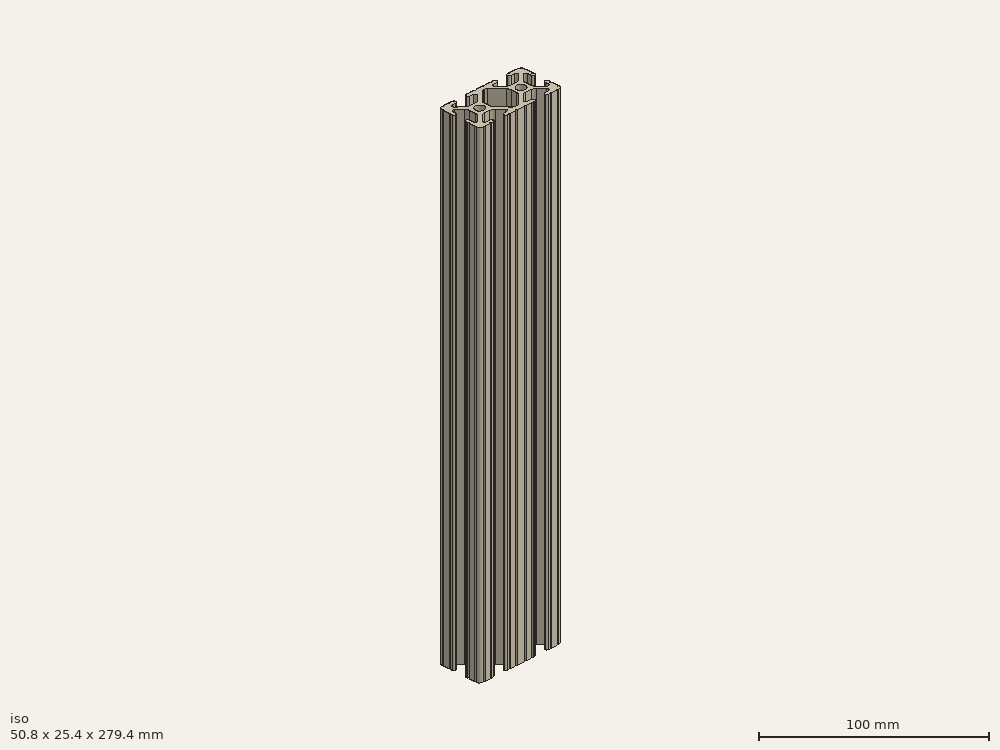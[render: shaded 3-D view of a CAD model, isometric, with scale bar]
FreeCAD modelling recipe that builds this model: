
FCSTD DOCUMENT  (FreeCAD 0.19R24267 (Git))
Label: 1020-11
License: All rights reserved
LicenseURL: http://en.wikipedia.org/wiki/All_rights_reserved
objects: Sketcher::SketchObject×1, Part::Extrusion×1
note: 2 computed .brp shape members not serialized (recipe doc carries the construction recipe); baked Part::Feature solids carry a one-line shape summary decoded from their .brp

FEATURE [Sketcher::SketchObject] Sketch162
  FullyConstrained = false
  sketch-geometry (162):
    g0: LineSegment StartX=7.25951 StartY=3.86941 StartZ=0 EndX=1.54575 EndY=9.57277 EndZ=0
    g1: LineSegment StartX=8.41248 StartY=-10.4902 StartZ=0 EndX=6.28364 EndY=-10.4902 EndZ=0
    g2: ArcOfCircle CenterX=8.41255 CenterY=-11.651 CenterZ=0 NormalX=0 NormalY=0 NormalZ=1 AngleXU=0 Radius=1.04895 StartAngle=4.71239 EndAngle=6.28319
    g3: LineSegment StartX=5.53258 StartY=-8.66607 StartZ=0 EndX=8.80999 EndY=-5.41626 EndZ=0
    g4: LineSegment StartX=9.4615 StartY=-11.651 StartZ=0 EndX=9.4615 EndY=-11.5392 EndZ=0
    g5: ArcOfCircle CenterX=8.41248 CenterY=-11.5392 CenterZ=0 NormalX=0 NormalY=0 NormalZ=1 AngleXU=0 Radius=1.04902 StartAngle=1.15714e-07 EndAngle=1.5708
    g6: ArcOfCircle CenterX=6.28364 CenterY=-9.42351 CenterZ=0 NormalX=0 NormalY=0 NormalZ=1 AngleXU=0 Radius=1.06669 StartAngle=2.35197 EndAngle=4.71239
    g7: LineSegment StartX=-7.28286 StartY=-3.84586 StartZ=0 EndX=-1.67557 EndY=-9.56109 EndZ=0
    g8: LineSegment StartX=1.50403 StartY=-9.57645 StartZ=0 EndX=7.25205 EndY=-3.87684 EndZ=0
    g9: LineSegment StartX=-0.551457 StartY=-10.033 StartZ=0 EndX=0.3952 EndY=-10.033 EndZ=0
    g10: LineSegment StartX=-1.54575 StartY=9.57277 StartZ=0 EndX=-7.25951 EndY=3.86941 EndZ=0
    g11: ArcOfCircle CenterX=0.3952 CenterY=-8.4582 CenterZ=0 NormalX=0 NormalY=0 NormalZ=1 AngleXU=0 Radius=1.5748 StartAngle=4.71239 EndAngle=5.49356
    g12: ArcOfCircle CenterX=5.0165 CenterY=-1.6223 CenterZ=0 NormalX=0 NormalY=0 NormalZ=1 AngleXU=0 Radius=3.175 StartAngle=5.49356 EndAngle=6.28319
    g13: LineSegment StartX=8.1915 StartY=-1.6223 StartZ=0 EndX=8.1915 EndY=1.6223 EndZ=0
    g14: LineSegment StartX=0.433213 StartY=10.033 StartZ=0 EndX=-0.433213 EndY=10.033 EndZ=0
    g15: ArcOfCircle CenterX=-0.551456 CenterY=-8.4582 CenterZ=0 NormalX=0 NormalY=0 NormalZ=1 AngleXU=0 Radius=1.5748 StartAngle=3.91746 EndAngle=4.71239
    g16: ArcOfCircle CenterX=-5.0165 CenterY=1.6223 CenterZ=0 NormalX=0 NormalY=0 NormalZ=1 AngleXU=0 Radius=3.175 StartAngle=2.35528 EndAngle=3.14159
    g17: ArcOfCircle CenterX=-0.433213 CenterY=8.4582 CenterZ=0 NormalX=0 NormalY=0 NormalZ=1 AngleXU=0 Radius=1.5748 StartAngle=1.5708 EndAngle=2.35528
    g18: ArcOfCircle CenterX=5.0165 CenterY=1.6223 CenterZ=0 NormalX=0 NormalY=0 NormalZ=1 AngleXU=0 Radius=3.175 StartAngle=2.15656e-07 EndAngle=0.78631
    g19: Circle CenterX=12.7 CenterY=-2.5e-15 CenterZ=0 NormalX=0 NormalY=0 NormalZ=-1 AngleXU=0 Radius=2.6035
    g20: Circle CenterX=-12.7 CenterY=2.5e-15 CenterZ=0 NormalX=0 NormalY=0 NormalZ=-1 AngleXU=0 Radius=2.6035
    g21: LineSegment StartX=-8.1915 StartY=1.6223 StartZ=0 EndX=-8.1915 EndY=-1.6223 EndZ=0
    g22: LineSegment StartX=-2.13358 StartY=-12.7 StartZ=0 EndX=2.13358 EndY=-12.7 EndZ=0
    g23: ArcOfCircle CenterX=-5.0165 CenterY=-1.6223 CenterZ=0 NormalX=0 NormalY=0 NormalZ=1 AngleXU=0 Radius=3.175 StartAngle=3.14159 EndAngle=3.91746
    g24: LineSegment StartX=3.14958 StartY=-12.7 StartZ=0 EndX=6.3669 EndY=-12.7 EndZ=0
    g25: ArcOfCircle CenterX=6.8749 CenterY=-12.7 CenterZ=0 NormalX=0 NormalY=0 NormalZ=1 AngleXU=0 Radius=0.508 StartAngle=0 EndAngle=3.14159
    g26: LineSegment StartX=-6.28939 StartY=-10.4902 StartZ=0 EndX=-8.41248 EndY=-10.4902 EndZ=0
    g27: LineSegment StartX=-8.41255 StartY=-12.7 StartZ=0 EndX=-7.38288 EndY=-12.7 EndZ=0
    g28: ArcOfCircle CenterX=0.433213 CenterY=8.4582 CenterZ=0 NormalX=0 NormalY=0 NormalZ=1 AngleXU=0 Radius=1.5748 StartAngle=0.78631 EndAngle=1.5708
    g29: ArcOfCircle CenterX=2.64158 CenterY=-12.7 CenterZ=0 NormalX=0 NormalY=0 NormalZ=1 AngleXU=0 Radius=0.508 StartAngle=0 EndAngle=3.14159
    g30: ArcOfCircle CenterX=-16.9875 CenterY=-11.5392 CenterZ=0 NormalX=0 NormalY=0 NormalZ=1 AngleXU=0 Radius=1.04902 StartAngle=1.16223e-07 EndAngle=1.5708
    g31: LineSegment StartX=-8.81696 StartY=-5.44724 StartZ=0 EndX=-5.56415 EndY=-8.76265 EndZ=0
    g32: LineSegment StartX=-16.9875 StartY=-10.4902 StartZ=0 EndX=-19.1164 EndY=-10.4902 EndZ=0
    g33: ArcOfCircle CenterX=-11.0833 CenterY=-7.6708 CenterZ=0 NormalX=0 NormalY=0 NormalZ=1 AngleXU=0 Radius=3.175 StartAngle=0.775866 EndAngle=1.5708
    g34: ArcOfCircle CenterX=-14.3449 CenterY=-7.6708 CenterZ=0 NormalX=0 NormalY=0 NormalZ=1 AngleXU=0 Radius=3.175 StartAngle=1.5708 EndAngle=2.3692
    g35: ArcOfCircle CenterX=-19.1164 CenterY=-9.4742 CenterZ=0 NormalX=0 NormalY=0 NormalZ=1 AngleXU=0 Radius=1.016 StartAngle=2.3692 EndAngle=4.71239
    g36: ArcOfCircle CenterX=-8.41248 CenterY=-11.5392 CenterZ=0 NormalX=0 NormalY=0 NormalZ=1 AngleXU=0 Radius=1.04902 StartAngle=1.5708 EndAngle=3.14159
    g37: LineSegment StartX=7.3829 StartY=-12.7 StartZ=0 EndX=8.41255 EndY=-12.7 EndZ=0
    g38: ArcOfCircle CenterX=-8.41255 CenterY=-11.651 CenterZ=0 NormalX=0 NormalY=0 NormalZ=1 AngleXU=0 Radius=1.04895 StartAngle=3.14159 EndAngle=4.71239
    g39: ArcOfCircle CenterX=14.3545 CenterY=-7.6708 CenterZ=0 NormalX=0 NormalY=0 NormalZ=1 AngleXU=0 Radius=3.175 StartAngle=0.789627 EndAngle=1.5708
    g40: ArcOfCircle CenterX=20.3835 CenterY=-1.55362 CenterZ=0 NormalX=0 NormalY=0 NormalZ=1 AngleXU=0 Radius=3.175 StartAngle=3.14159 EndAngle=3.93122
    g41: LineSegment StartX=23.1902 StartY=6.498 StartZ=0 EndX=23.1902 EndY=4.28752 EndZ=0
    g42: LineSegment StartX=-14.3449 StartY=-4.4958 StartZ=0 EndX=-11.0833 EndY=-4.4958 EndZ=0
    g43: LineSegment StartX=-19.8441 StartY=-8.76517 StartZ=0 EndX=-16.619 EndY=-5.45511 EndZ=0
    g44: LineSegment StartX=-6.36688 StartY=-12.7 StartZ=0 EndX=-3.14958 EndY=-12.7 EndZ=0
    g45: ArcOfCircle CenterX=-6.28939 CenterY=-9.4742 CenterZ=0 NormalX=0 NormalY=0 NormalZ=1 AngleXU=0 Radius=1.016 StartAngle=4.71239 EndAngle=7.05905
    g46: LineSegment StartX=-9.4615 StartY=-11.5392 StartZ=0 EndX=-9.4615 EndY=-11.6511 EndZ=0
    g47: ArcOfCircle CenterX=-6.87488 CenterY=-12.7 CenterZ=0 NormalX=0 NormalY=0 NormalZ=1 AngleXU=0 Radius=0.508 StartAngle=0 EndAngle=3.14159
    g48: LineSegment StartX=-15.9385 StartY=-11.651 StartZ=0 EndX=-15.9385 EndY=-11.5392 EndZ=0
    g49: ArcOfCircle CenterX=-2.64158 CenterY=-12.7 CenterZ=0 NormalX=0 NormalY=0 NormalZ=1 AngleXU=0 Radius=0.508 StartAngle=0 EndAngle=3.14159
    g50: ArcOfCircle CenterX=22.1596 CenterY=-6.33474 CenterZ=0 NormalX=0 NormalY=0 NormalZ=1 AngleXU=0 Radius=1.03057 StartAngle=3.93122 EndAngle=6.28319
    g51: ArcOfCircle CenterX=25.4 CenterY=5.82513 CenterZ=0 NormalX=0 NormalY=0 NormalZ=1 AngleXU=0 Radius=0.508 StartAngle=1.5708 EndAngle=4.71239
    g52: LineSegment StartX=25.4 StartY=6.33313 StartZ=0 EndX=25.4 EndY=9.5504 EndZ=0
    g53: LineSegment StartX=19.0331 StartY=-12.7 StartZ=0 EndX=22.2504 EndY=-12.7 EndZ=0
    g54: ArcOfCircle CenterX=20.3835 CenterY=1.69518 CenterZ=0 NormalX=0 NormalY=0 NormalZ=1 AngleXU=0 Radius=3.175 StartAngle=2.35528 EndAngle=3.14159
    g55: LineSegment StartX=16.9875 StartY=-12.7 StartZ=0 EndX=18.0171 EndY=-12.7 EndZ=0
    g56: ArcOfCircle CenterX=23.2918 CenterY=10.5918 CenterZ=0 NormalX=0 NormalY=0 NormalZ=1 AngleXU=0 Radius=2.1082 StartAngle=6.27114 EndAngle=7.86603
    g57: ArcOfCircle CenterX=24.2392 CenterY=-4.28752 CenterZ=0 NormalX=0 NormalY=0 NormalZ=1 AngleXU=0 Radius=1.04902 StartAngle=1.5708 EndAngle=3.14159
    g58: ArcOfCircle CenterX=24.401 CenterY=-4.23752 CenterZ=0 NormalX=0 NormalY=0 NormalZ=1 AngleXU=0 Radius=0.99902 StartAngle=1.41033e-07 EndAngle=1.5708
    g59: LineSegment StartX=16.59 StartY=-5.41626 StartZ=0 EndX=19.8674 EndY=-8.66607 EndZ=0
    g60: ArcOfCircle CenterX=16.9875 CenterY=-11.5392 CenterZ=0 NormalX=0 NormalY=0 NormalZ=1 AngleXU=0 Radius=1.04902 StartAngle=1.5708 EndAngle=3.14159
    g61: LineSegment StartX=22.2504 StartY=12.7 StartZ=0 EndX=19.0331 EndY=12.7 EndZ=0
    g62: ArcOfCircle CenterX=23.2918 CenterY=-10.5918 CenterZ=0 NormalX=0 NormalY=0 NormalZ=1 AngleXU=0 Radius=2.1082 StartAngle=4.70034 EndAngle=6.29523
    g63: ArcOfCircle CenterX=11.0455 CenterY=-7.6708 CenterZ=0 NormalX=0 NormalY=0 NormalZ=1 AngleXU=0 Radius=3.175 StartAngle=1.5708 EndAngle=2.35197
    g64: ArcOfCircle CenterX=22.7584 CenterY=12.7 CenterZ=0 NormalX=0 NormalY=0 NormalZ=1 AngleXU=0 Radius=0.508 StartAngle=3.14159 EndAngle=6.28288
    g65: LineSegment StartX=19.1164 StartY=-10.4902 StartZ=0 EndX=16.9875 EndY=-10.4902 EndZ=0
    g66: ArcOfCircle CenterX=22.7584 CenterY=-12.7 CenterZ=0 NormalX=0 NormalY=0 NormalZ=1 AngleXU=0 Radius=0.508 StartAngle=0.000301216 EndAngle=3.14159
    g67: ArcOfCircle CenterX=16.9875 CenterY=11.651 CenterZ=0 NormalX=0 NormalY=0 NormalZ=1 AngleXU=0 Radius=1.04902 StartAngle=1.5708 EndAngle=3.14159
    g68: ArcOfCircle CenterX=24.351 CenterY=4.28752 CenterZ=0 NormalX=0 NormalY=0 NormalZ=1 AngleXU=0 Radius=1.04902 StartAngle=4.71239 EndAngle=6.28319
    g69: ArcOfCircle CenterX=19.1164 CenterY=9.4742 CenterZ=0 NormalX=0 NormalY=0 NormalZ=1 AngleXU=0 Radius=1.016 StartAngle=5.49688 EndAngle=7.85398
    g70: LineSegment StartX=19.8341 StartY=8.75512 StartZ=0 EndX=16.4966 EndY=5.42369 EndZ=0
    g71: LineSegment StartX=18.0171 StartY=12.7 StartZ=0 EndX=16.9875 EndY=12.7 EndZ=0
    g72: ArcOfCircle CenterX=18.5251 CenterY=-12.7 CenterZ=0 NormalX=0 NormalY=0 NormalZ=1 AngleXU=0 Radius=0.508 StartAngle=0 EndAngle=3.14159
    g73: LineSegment StartX=15.9384 StartY=11.651 StartZ=0 EndX=15.9384 EndY=11.5392 EndZ=0
    g74: LineSegment StartX=16.9875 StartY=10.4902 StartZ=0 EndX=19.1164 EndY=10.4902 EndZ=0
    g75: LineSegment StartX=11.0455 StartY=-4.4958 StartZ=0 EndX=14.3545 EndY=-4.4958 EndZ=0
    g76: ArcOfCircle CenterX=14.2536 CenterY=7.6708 CenterZ=0 NormalX=0 NormalY=0 NormalZ=1 AngleXU=0 Radius=3.175 StartAngle=4.71239 EndAngle=5.49688
    g77: ArcOfCircle CenterX=25.4 CenterY=-5.82508 CenterZ=0 NormalX=0 NormalY=0 NormalZ=1 AngleXU=0 Radius=0.508 StartAngle=1.5708 EndAngle=4.71239
    g78: LineSegment StartX=18.1405 StartY=3.94229 StartZ=0 EndX=21.4316 EndY=7.22739 EndZ=0
    g79: LineSegment StartX=25.4 StartY=-5.31708 StartZ=0 EndX=25.4 EndY=-4.23752 EndZ=0
    g80: LineSegment StartX=14.2536 StartY=4.4958 StartZ=0 EndX=11.1464 EndY=4.4958 EndZ=0
    g81: ArcOfCircle CenterX=18.5251 CenterY=12.7 CenterZ=0 NormalX=0 NormalY=0 NormalZ=1 AngleXU=0 Radius=0.508 StartAngle=3.14159 EndAngle=6.28319
    g82: LineSegment StartX=23.1902 StartY=-4.28752 StartZ=0 EndX=23.1902 EndY=-6.33474 EndZ=0
    g83: LineSegment StartX=24.401 StartY=-3.2385 StartZ=0 EndX=24.2392 EndY=-3.2385 EndZ=0
    g84: ArcOfCircle CenterX=22.1596 CenterY=6.498 CenterZ=0 NormalX=0 NormalY=0 NormalZ=1 AngleXU=0 Radius=1.03057 StartAngle=0 EndAngle=2.35528
    g85: LineSegment StartX=15.9385 StartY=-11.5392 StartZ=0 EndX=15.9385 EndY=-11.6511 EndZ=0
    g86: LineSegment StartX=25.4 StartY=4.28752 StartZ=0 EndX=25.4 EndY=5.31713 EndZ=0
    g87: ArcOfCircle CenterX=11.1464 CenterY=7.6708 CenterZ=0 NormalX=0 NormalY=0 NormalZ=1 AngleXU=0 Radius=3.175 StartAngle=3.9279 EndAngle=4.71239
    g88: LineSegment StartX=8.90339 StartY=5.42369 StartZ=0 EndX=5.56588 EndY=8.75512 EndZ=0
    g89: LineSegment StartX=21.434 StartY=-7.06654 StartZ=0 EndX=18.148 EndY=-3.80816 EndZ=0
    g90: ArcOfCircle CenterX=25.4 CenterY=10.0584 CenterZ=0 NormalX=0 NormalY=0 NormalZ=1 AngleXU=0 Radius=0.508 StartAngle=1.5711 EndAngle=4.71239
    g91: ArcOfCircle CenterX=16.9875 CenterY=-11.651 CenterZ=0 NormalX=0 NormalY=0 NormalZ=1 AngleXU=0 Radius=1.04895 StartAngle=3.14159 EndAngle=4.71239
    g92: ArcOfCircle CenterX=19.1164 CenterY=-9.42352 CenterZ=0 NormalX=0 NormalY=0 NormalZ=1 AngleXU=0 Radius=1.06668 StartAngle=4.71239 EndAngle=7.07281
    g93: ArcOfCircle CenterX=24.2392 CenterY=4.28752 CenterZ=0 NormalX=0 NormalY=0 NormalZ=1 AngleXU=0 Radius=1.04902 StartAngle=3.14159 EndAngle=4.71239
    g94: ArcOfCircle CenterX=16.9875 CenterY=11.5392 CenterZ=0 NormalX=0 NormalY=0 NormalZ=1 AngleXU=0 Radius=1.04902 StartAngle=3.14159 EndAngle=4.71239
    g95: ArcOfCircle CenterX=25.4 CenterY=-10.0584 CenterZ=0 NormalX=0 NormalY=0 NormalZ=1 AngleXU=0 Radius=0.508 StartAngle=1.5708 EndAngle=4.71209
    g96: ArcOfCircle CenterX=6.87487 CenterY=12.7 CenterZ=0 NormalX=0 NormalY=0 NormalZ=1 AngleXU=0 Radius=0.508 StartAngle=3.14159 EndAngle=6.28319
    g97: LineSegment StartX=25.4 StartY=-9.5504 StartZ=0 EndX=25.4 EndY=-6.33308 EndZ=0
    g98: LineSegment StartX=17.2085 StartY=-1.55362 StartZ=0 EndX=17.2085 EndY=1.69518 EndZ=0
    g99: LineSegment StartX=-9.46155 StartY=11.651 StartZ=0 EndX=-9.46155 EndY=11.5392 EndZ=0
    g100: LineSegment StartX=24.2392 StartY=3.2385 StartZ=0 EndX=24.351 EndY=3.2385 EndZ=0
    g101: LineSegment StartX=-8.41253 StartY=10.4902 StartZ=0 EndX=-6.28939 EndY=10.4902 EndZ=0
    g102: ArcOfCircle CenterX=-10.8409 CenterY=7.6708 CenterZ=0 NormalX=0 NormalY=0 NormalZ=1 AngleXU=0 Radius=3.175 StartAngle=4.71239 EndAngle=5.49688
    g103: LineSegment StartX=-19.1164 StartY=10.4902 StartZ=0 EndX=-16.9875 EndY=10.4902 EndZ=0
    g104: LineSegment StartX=-10.8409 StartY=4.4958 StartZ=0 EndX=-14.1026 EndY=4.4958 EndZ=0
    g105: LineSegment StartX=-16.1879 StartY=5.27664 StartZ=0 EndX=-19.8682 EndY=8.48225 EndZ=0
    g106: LineSegment StartX=-7.38291 StartY=12.7 StartZ=0 EndX=-8.41253 EndY=12.7 EndZ=0
    g107: ArcOfCircle CenterX=-6.28939 CenterY=9.34546 CenterZ=0 NormalX=0 NormalY=0 NormalZ=1 AngleXU=0 Radius=1.14474 StartAngle=5.49688 EndAngle=7.85398
    g108: LineSegment StartX=6.28364 StartY=10.4902 StartZ=0 EndX=8.41253 EndY=10.4902 EndZ=0
    g109: ArcOfCircle CenterX=8.41253 CenterY=11.651 CenterZ=0 NormalX=0 NormalY=0 NormalZ=1 AngleXU=0 Radius=1.04902 StartAngle=4.29175e-07 EndAngle=1.5708
    g110: LineSegment StartX=9.46155 StartY=11.5392 StartZ=0 EndX=9.46155 EndY=11.651 EndZ=0
    g111: ArcOfCircle CenterX=-14.1026 CenterY=7.6708 CenterZ=0 NormalX=0 NormalY=0 NormalZ=1 AngleXU=0 Radius=3.175 StartAngle=3.99583 EndAngle=4.71239
    g112: LineSegment StartX=-5.48068 StartY=8.53527 StartZ=0 EndX=-8.59793 EndY=5.42369 EndZ=0
    g113: ArcOfCircle CenterX=-19.1164 CenterY=9.34546 CenterZ=0 NormalX=0 NormalY=0 NormalZ=1 AngleXU=0 Radius=1.14474 StartAngle=1.5708 EndAngle=3.99583
    g114: LineSegment StartX=8.41253 StartY=12.7 StartZ=0 EndX=7.38287 EndY=12.7 EndZ=0
    g115: LineSegment StartX=-3.14958 StartY=12.7 StartZ=0 EndX=-6.36691 EndY=12.7 EndZ=0
    g116: ArcOfCircle CenterX=-8.41253 CenterY=11.5392 CenterZ=0 NormalX=0 NormalY=0 NormalZ=1 AngleXU=0 Radius=1.04902 StartAngle=3.14159 EndAngle=4.71239
    g117: ArcOfCircle CenterX=8.41253 CenterY=11.5392 CenterZ=0 NormalX=0 NormalY=0 NormalZ=1 AngleXU=0 Radius=1.04902 StartAngle=4.71239 EndAngle=6.28319
    g118: ArcOfCircle CenterX=-6.87491 CenterY=12.7 CenterZ=0 NormalX=0 NormalY=0 NormalZ=1 AngleXU=0 Radius=0.508 StartAngle=3.14159 EndAngle=6.28319
    g119: ArcOfCircle CenterX=-8.41253 CenterY=11.651 CenterZ=0 NormalX=0 NormalY=0 NormalZ=1 AngleXU=0 Radius=1.04902 StartAngle=1.5708 EndAngle=3.14159
    g120: ArcOfCircle CenterX=-2.64159 CenterY=12.7 CenterZ=0 NormalX=0 NormalY=0 NormalZ=1 AngleXU=0 Radius=0.507987 StartAngle=3.14159 EndAngle=6.28319
    g121: ArcOfCircle CenterX=6.28364 CenterY=9.4742 CenterZ=0 NormalX=0 NormalY=0 NormalZ=1 AngleXU=0 Radius=1.016 StartAngle=1.5708 EndAngle=3.9279
    g122: LineSegment StartX=2.13361 StartY=12.7 StartZ=0 EndX=-2.13361 EndY=12.7 EndZ=0
    g123: LineSegment StartX=6.36687 StartY=12.7 StartZ=0 EndX=3.14961 EndY=12.7 EndZ=0
    g124: ArcOfCircle CenterX=-24.401 CenterY=4.23752 CenterZ=0 NormalX=0 NormalY=0 NormalZ=1 AngleXU=0 Radius=0.99902 StartAngle=3.14159 EndAngle=4.71239
    g125: LineSegment StartX=-16.9875 StartY=12.7 StartZ=0 EndX=-18.0171 EndY=12.7 EndZ=0
    g126: LineSegment StartX=-24.401 StartY=3.2385 StartZ=0 EndX=-24.1892 EndY=3.2385 EndZ=0
    g127: ArcOfCircle CenterX=2.64161 CenterY=12.7 CenterZ=0 NormalX=0 NormalY=0 NormalZ=1 AngleXU=0 Radius=0.508 StartAngle=3.14159 EndAngle=6.28319
    g128: ArcOfCircle CenterX=-22.2207 CenterY=-6.67687 CenterZ=0 NormalX=0 NormalY=0 NormalZ=1 AngleXU=0 Radius=0.969476 StartAngle=3.14159 EndAngle=5.51079
    g129: LineSegment StartX=-18.1094 StartY=-3.8465 StartZ=0 EndX=-21.5263 EndY=-7.35342 EndZ=0
    g130: LineSegment StartX=-17.2085 StartY=1.63081 StartZ=0 EndX=-17.2085 EndY=-1.63081 EndZ=0
    g131: ArcOfCircle CenterX=-22.2207 CenterY=6.15588 CenterZ=0 NormalX=0 NormalY=0 NormalZ=1 AngleXU=0 Radius=0.969476 StartAngle=0.854233 EndAngle=3.14159
    g132: LineSegment StartX=-24.1892 StartY=-3.2385 StartZ=0 EndX=-24.401 EndY=-3.2385 EndZ=0
    g133: ArcOfCircle CenterX=-25.4 CenterY=10.0584 CenterZ=0 NormalX=0 NormalY=0 NormalZ=1 AngleXU=0 Radius=0.508 StartAngle=4.71239 EndAngle=7.85368
    g134: LineSegment StartX=-23.1902 StartY=-6.67687 StartZ=0 EndX=-23.1902 EndY=-4.23752 EndZ=0
    g135: ArcOfCircle CenterX=-20.3835 CenterY=-1.63081 CenterZ=0 NormalX=0 NormalY=0 NormalZ=1 AngleXU=0 Radius=3.175 StartAngle=5.51079 EndAngle=6.28319
    g136: ArcOfCircle CenterX=-24.1892 CenterY=-4.23752 CenterZ=0 NormalX=0 NormalY=0 NormalZ=1 AngleXU=0 Radius=0.99902 StartAngle=1.41033e-07 EndAngle=1.5708
    g137: ArcOfCircle CenterX=-25.4 CenterY=5.82508 CenterZ=0 NormalX=0 NormalY=0 NormalZ=1 AngleXU=0 Radius=0.508 StartAngle=4.71239 EndAngle=7.85398
    g138: LineSegment StartX=-23.1902 StartY=4.23752 StartZ=0 EndX=-23.1902 EndY=6.15588 EndZ=0
    g139: LineSegment StartX=-15.9384 StartY=11.5392 StartZ=0 EndX=-15.9384 EndY=11.651 EndZ=0
    g140: ArcOfCircle CenterX=-22.7584 CenterY=12.7 CenterZ=0 NormalX=0 NormalY=0 NormalZ=1 AngleXU=0 Radius=0.508 StartAngle=3.14189 EndAngle=6.28319
    g141: LineSegment StartX=-19.0331 StartY=12.7 StartZ=0 EndX=-22.2504 EndY=12.7 EndZ=0
    g142: ArcOfCircle CenterX=-16.9875 CenterY=11.651 CenterZ=0 NormalX=0 NormalY=0 NormalZ=1 AngleXU=0 Radius=1.04902 StartAngle=4.28571e-07 EndAngle=1.5708
    g143: ArcOfCircle CenterX=-18.5251 CenterY=12.7 CenterZ=0 NormalX=0 NormalY=0 NormalZ=1 AngleXU=0 Radius=0.508 StartAngle=3.14159 EndAngle=6.28319
    g144: ArcOfCircle CenterX=-24.1892 CenterY=4.23752 CenterZ=0 NormalX=0 NormalY=0 NormalZ=1 AngleXU=0 Radius=0.99902 StartAngle=4.71239 EndAngle=6.28319
    g145: LineSegment StartX=-25.4 StartY=5.31708 StartZ=0 EndX=-25.4 EndY=4.23752 EndZ=0
    g146: ArcOfCircle CenterX=-16.9875 CenterY=11.5392 CenterZ=0 NormalX=0 NormalY=0 NormalZ=1 AngleXU=0 Radius=1.04902 StartAngle=4.71239 EndAngle=6.28319
    g147: LineSegment StartX=-21.584 StartY=6.88693 StartZ=0 EndX=-18.2982 EndY=4.02497 EndZ=0
    g148: ArcOfCircle CenterX=-20.3835 CenterY=1.63081 CenterZ=0 NormalX=0 NormalY=0 NormalZ=1 AngleXU=0 Radius=3.175 StartAngle=0 EndAngle=0.854233
    g149: ArcOfCircle CenterX=-23.2918 CenterY=10.5918 CenterZ=0 NormalX=0 NormalY=0 NormalZ=1 AngleXU=0 Radius=2.1082 StartAngle=1.55875 EndAngle=3.15364
    g150: LineSegment StartX=-25.4 StartY=9.5504 StartZ=0 EndX=-25.4 EndY=6.33308 EndZ=0
    g151: LineSegment StartX=-25.4 StartY=-4.23752 StartZ=0 EndX=-25.4 EndY=-5.31708 EndZ=0
    g152: ArcOfCircle CenterX=-23.2918 CenterY=-10.5918 CenterZ=0 NormalX=0 NormalY=0 NormalZ=1 AngleXU=0 Radius=2.1082 StartAngle=3.12954 EndAngle=4.72444
    g153: ArcOfCircle CenterX=-22.7584 CenterY=-12.7 CenterZ=0 NormalX=0 NormalY=0 NormalZ=1 AngleXU=0 Radius=0.508 StartAngle=0 EndAngle=3.14129
    g154: LineSegment StartX=-18.0171 StartY=-12.7 StartZ=0 EndX=-16.9875 EndY=-12.7 EndZ=0
    g155: ArcOfCircle CenterX=-25.4 CenterY=-10.0584 CenterZ=0 NormalX=0 NormalY=0 NormalZ=1 AngleXU=0 Radius=0.508 StartAngle=4.71269 EndAngle=7.85398
    g156: LineSegment StartX=-22.2504 StartY=-12.7 StartZ=0 EndX=-19.0331 EndY=-12.7 EndZ=0
    g157: ArcOfCircle CenterX=-16.9875 CenterY=-11.651 CenterZ=0 NormalX=0 NormalY=0 NormalZ=1 AngleXU=0 Radius=1.04895 StartAngle=4.71239 EndAngle=6.28319
    g158: ArcOfCircle CenterX=-24.401 CenterY=-4.23752 CenterZ=0 NormalX=0 NormalY=0 NormalZ=1 AngleXU=0 Radius=0.99902 StartAngle=1.5708 EndAngle=3.14159
    g159: ArcOfCircle CenterX=-25.4 CenterY=-5.82513 CenterZ=0 NormalX=0 NormalY=0 NormalZ=1 AngleXU=0 Radius=0.508051 StartAngle=4.71239 EndAngle=7.85398
    g160: ArcOfCircle CenterX=-18.5251 CenterY=-12.7 CenterZ=0 NormalX=0 NormalY=0 NormalZ=1 AngleXU=0 Radius=0.508 StartAngle=0 EndAngle=3.14159
    g161: LineSegment StartX=-25.4 StartY=-6.33319 StartZ=0 EndX=-25.4 EndY=-9.5504 EndZ=0
  constraints (160):
    c: Coincident(g161,g155)
    c: Coincident(g159,g161)
    c: Coincident(g151,g159)
    c: Coincident(g158,g151)
    c: Coincident(g124,g145)
    c: Coincident(g137,g145)
    c: Coincident(g137,g150)
    c: Coincident(g133,g150)
    c: Coincident(g152,g155)
    c: Coincident(g149,g133)
    c: Coincident(g158,g132)
    c: Coincident(g124,g126)
    c: Coincident(g136,g132)
    c: Coincident(g144,g126)
    c: Coincident(g153,g152)
    c: Coincident(g140,g149)
    c: Coincident(g134,g128)
    c: Coincident(g134,g136)
    c: Coincident(g138,g144)
    c: Coincident(g131,g138)
    c: Coincident(g153,g156)
    c: Coincident(g141,g140)
    c: Coincident(g131,g147)
    c: Coincident(g129,g128)
    c: Coincident(g105,g113)
    c: Coincident(g35,g43)
    c: Coincident(g35,g32)
    c: Coincident(g113,g103)
    c: Coincident(g156,g160)
    c: Coincident(g143,g141)
    c: Coincident(g147,g148)
    c: Coincident(g135,g129)
    c: Coincident(g154,g160)
    c: Coincident(g143,g125)
    c: Coincident(g130,g135)
    c: Coincident(g130,g148)
    c: Coincident(g154,g157)
    c: Coincident(g32,g30)
    c: Coincident(g103,g146)
    c: Coincident(g142,g125)
    c: Coincident(g43,g34)
    c: Coincident(g111,g105)
    c: Coincident(g157,g48)
    c: Coincident(g48,g30)
    c: Coincident(g139,g146)
    c: Coincident(g139,g142)
    c: Coincident(g42,g34)
    c: Coincident(g104,g111)
    c: Coincident(g33,g42)
    c: Coincident(g102,g104)
    c: Coincident(g38,g46)
    c: Coincident(g46,g36)
    c: Coincident(g99,g116)
    c: Coincident(g119,g99)
    c: Coincident(g33,g31)
    c: Coincident(g102,g112)
    c: Coincident(g27,g38)
    c: Coincident(g36,g26)
    c: Coincident(g116,g101)
    c: Coincident(g106,g119)
    c: Coincident(g21,g23)
    c: Coincident(g21,g16)
    c: Coincident(g27,g47)
    c: Coincident(g106,g118)
    c: Coincident(g23,g7)
    c: Coincident(g10,g16)
    c: Coincident(g44,g47)
    c: Coincident(g118,g115)
    c: Coincident(g45,g26)
    c: Coincident(g107,g101)
    c: Coincident(g45,g31)
    c: Coincident(g112,g107)
    c: Coincident(g44,g49)
    c: Coincident(g120,g115)
    c: Coincident(g22,g49)
    c: Coincident(g122,g120)
    c: Coincident(g15,g7)
    c: Coincident(g10,g17)
    c: Coincident(g9,g15)
    c: Coincident(g17,g14)
    c: Coincident(g9,g11)
    c: Coincident(g14,g28)
    c: Coincident(g8,g11)
    c: Coincident(g0,g28)
    c: Coincident(g29,g22)
    c: Coincident(g122,g127)
    c: Coincident(g24,g29)
    c: Coincident(g123,g127)
    c: Coincident(g3,g6)
    c: Coincident(g88,g121)
    c: Coincident(g1,g6)
    c: Coincident(g108,g121)
    c: Coincident(g25,g24)
    c: Coincident(g96,g123)
    c: Coincident(g8,g12)
    c: Coincident(g18,g0)
    c: Coincident(g25,g37)
    c: Coincident(g96,g114)
    c: Coincident(g12,g13)
    c: Coincident(g18,g13)
    c: Coincident(g2,g37)
    c: Coincident(g5,g1)
    c: Coincident(g117,g108)
    c: Coincident(g109,g114)
    c: Coincident(g3,g63)
    c: Coincident(g87,g88)
    c: Coincident(g2,g4)
    c: Coincident(g5,g4)
    c: Coincident(g117,g110)
    c: Coincident(g109,g110)
    c: Coincident(g75,g63)
    c: Coincident(g80,g87)
    c: Coincident(g80,g76)
    c: Coincident(g39,g75)
    c: Coincident(g85,g91)
    c: Coincident(g85,g60)
    c: Coincident(g73,g94)
    c: Coincident(g73,g67)
    c: Coincident(g70,g76)
    c: Coincident(g59,g39)
    c: Coincident(g55,g91)
    c: Coincident(g60,g65)
    c: Coincident(g94,g74)
    c: Coincident(g67,g71)
    c: Coincident(g40,g98)
    c: Coincident(g54,g98)
    c: Coincident(g55,g72)
    c: Coincident(g71,g81)
    c: Coincident(g78,g54)
    c: Coincident(g40,g89)
    c: Coincident(g53,g72)
    c: Coincident(g61,g81)
    c: Coincident(g65,g92)
    c: Coincident(g74,g69)
    c: Coincident(g70,g69)
    c: Coincident(g59,g92)
    c: Coincident(g84,g78)
    c: Coincident(g50,g89)
    c: Coincident(g53,g66)
    c: Coincident(g64,g61)
    c: Coincident(g82,g50)
    c: Coincident(g57,g82)
    c: Coincident(g41,g93)
    c: Coincident(g41,g84)
    c: Coincident(g62,g66)
    c: Coincident(g64,g56)
    c: Coincident(g57,g83)
    c: Coincident(g100,g93)
    c: Coincident(g100,g68)
    c: Coincident(g58,g83)
    c: Coincident(g62,g95)
    c: Coincident(g56,g90)
    c: Coincident(g97,g95)
    c: Coincident(g97,g77)
    c: Coincident(g77,g79)
    c: Coincident(g58,g79)
    c: Coincident(g68,g86)
    c: Coincident(g86,g51)
    c: Coincident(g51,g52)
    c: Coincident(g52,g90)
FEATURE [Part::Extrusion] Extrude
  Base = -> Sketch162
  Dir = (0,0,1)
  DirMode = 2
  FaceMakerClass = Part::FaceMakerBullseye
  LengthFwd = 279.4
  LengthRev = 0
  Solid = true
  Symmetric = false
